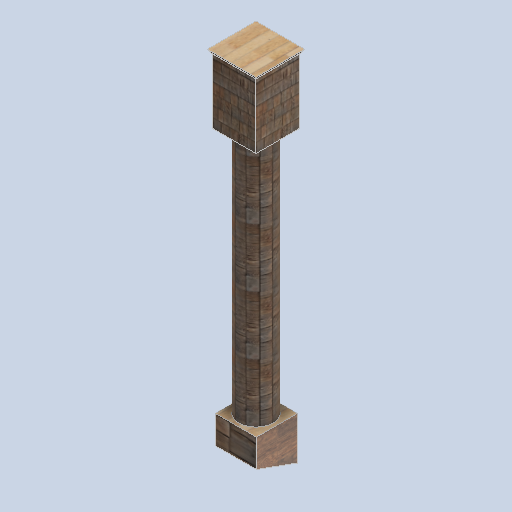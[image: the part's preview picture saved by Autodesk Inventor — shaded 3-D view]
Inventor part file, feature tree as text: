
AUTODESK INVENTOR PART (.ipt)
format: ipt  version: 2024.2 (Build 282272000, 272)  size: 384,512 bytes
history: native  units: mm
features: sketch x5, extrude x4, plane x2
ambient origin geometry x8: Origin, YZ Plane, XZ Plane, XY Plane, X Axis, Y Axis, Z Axis, Center Point
bodies: Solid1 (feature_tree)
feature tree (11):
  sketch  "Sketch1"  dims[d0=239.0mm d2=0.0mm d3=90.0deg]
  plane  "Work Plane3"
  extrude  "Extrusion1"  TaperAngle=0.0deg  [1 undecoded]
  extrude  "Extrusion2"  Depth=3000.0mm
  extrude  "Extrusion3"  Depth=250.0mm
  extrude  "Extrusion4"  Depth=239.0mm
  plane  "Work Plane2"
  sketch  "Sketch2"  dims[d4=3000.0mm d5=3000.0mm]
  sketch  "Sketch3"  dims[d6=3.490659mm d7=250.0mm]
  sketch  "Sketch4"  dims[d8=239.0mm d9=0.0mm d10=200.0mm]
  sketch  "Sketch5"  dims[d11=1431.0mm d12=0.0mm d13=250.0mm d14=250.0mm d15=380.0mm d16=0.0mm d17=260.0mm d18=260.0mm d19=20.0mm d20=30.0deg]
note: 1 required parameter value undecoded (feature->parameter linkage not recoverable at this tier; creation-order binding heuristic only, values carry confidence <= 0.55)
